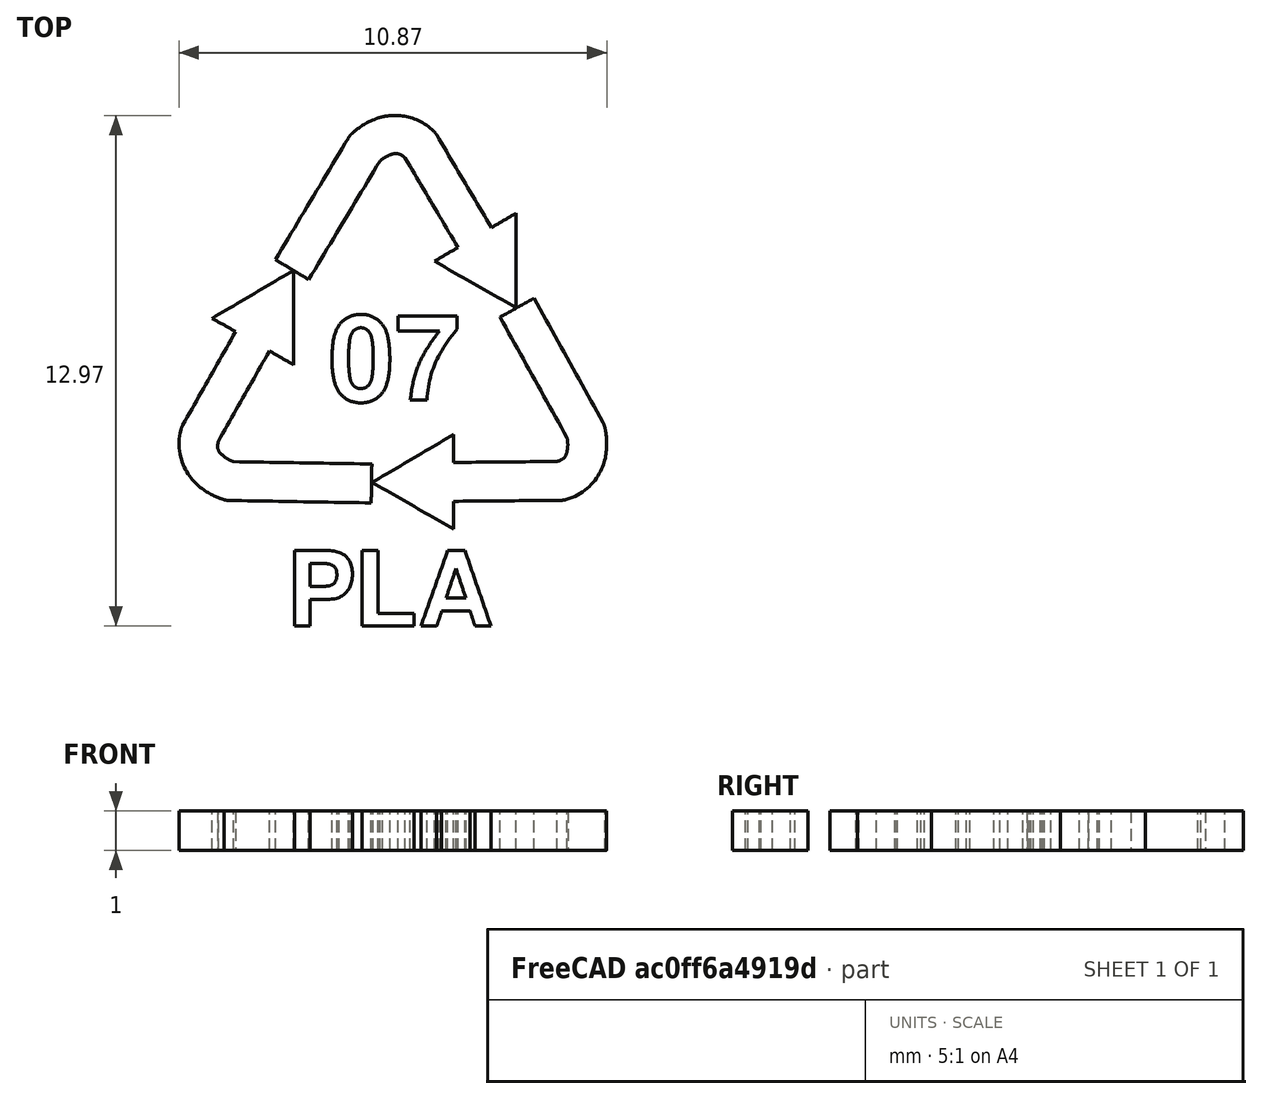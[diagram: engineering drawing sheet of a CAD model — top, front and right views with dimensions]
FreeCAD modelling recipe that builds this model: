
FCSTD DOCUMENT  (FreeCAD 0.18.4R)
Label: PLA
License: All rights reserved
LicenseURL: http://en.wikipedia.org/wiki/All_rights_reserved
objects: Part::Feature×7, Part::Extrusion×1, Part::MultiFuse×1, Part::FeaturePython×1, App::DocumentObjectGroup×1
note: 10 computed .brp shape members not serialized (recipe doc carries the construction recipe); baked Part::Feature solids carry a one-line shape summary decoded from their .brp

FEATURE [Part::Feature] path860
  shape: bbox 2.938 x 4.497 x 2e-07 mm, 1 faces, 0 solids (baked)
FEATURE [Part::Feature] path860001
  shape: bbox 1.252 x 3.095 x 2e-07 mm, 1 faces, 0 solids (baked)
FEATURE [Part::Feature] path853
  shape: bbox 2.934 x 3.84 x 2e-07 mm, 1 faces, 0 solids (baked)
FEATURE [Part::Feature] path853001
  shape: bbox 1.354 x 1.154 x 2e-07 mm, 1 faces, 0 solids (baked)
FEATURE [Part::Feature] path857
  shape: bbox 3.567 x 3.84 x 2e-07 mm, 1 faces, 0 solids (baked)
FEATURE [Part::Feature] path857001
  shape: bbox 1.001 x 1.501 x 2e-07 mm, 1 faces, 0 solids (baked)
FEATURE [Part::Feature] Shell
  shape: bbox 22.06 x 26.01 x 2e-07 mm, 11 faces, 0 solids (baked)
FEATURE [Part::Extrusion] Extrude
  Base = -> Shell
  Dir = (0,0,1)
  DirMode = 0
  FaceMakerClass = Part::FaceMakerBullseye
  LengthFwd = 1
  LengthRev = 0
  Solid = true
  Symmetric = false
FEATURE [Part::MultiFuse] Fusion
  Refine = true
  Shapes = -> [Extrude]
FEATURE [Part::FeaturePython] Scale  label="Sign_PLA"  # Draft clone (typed FeaturePython)
  Fuse = false
  Objects = -> [Fusion]
  Scale = (0.5,0.5,1)
FEATURE [App::DocumentObjectGroup] Group  label="Helpers"
  Group = -> [path853,path853001,path857,path857001,path860,path860001,Fusion]
